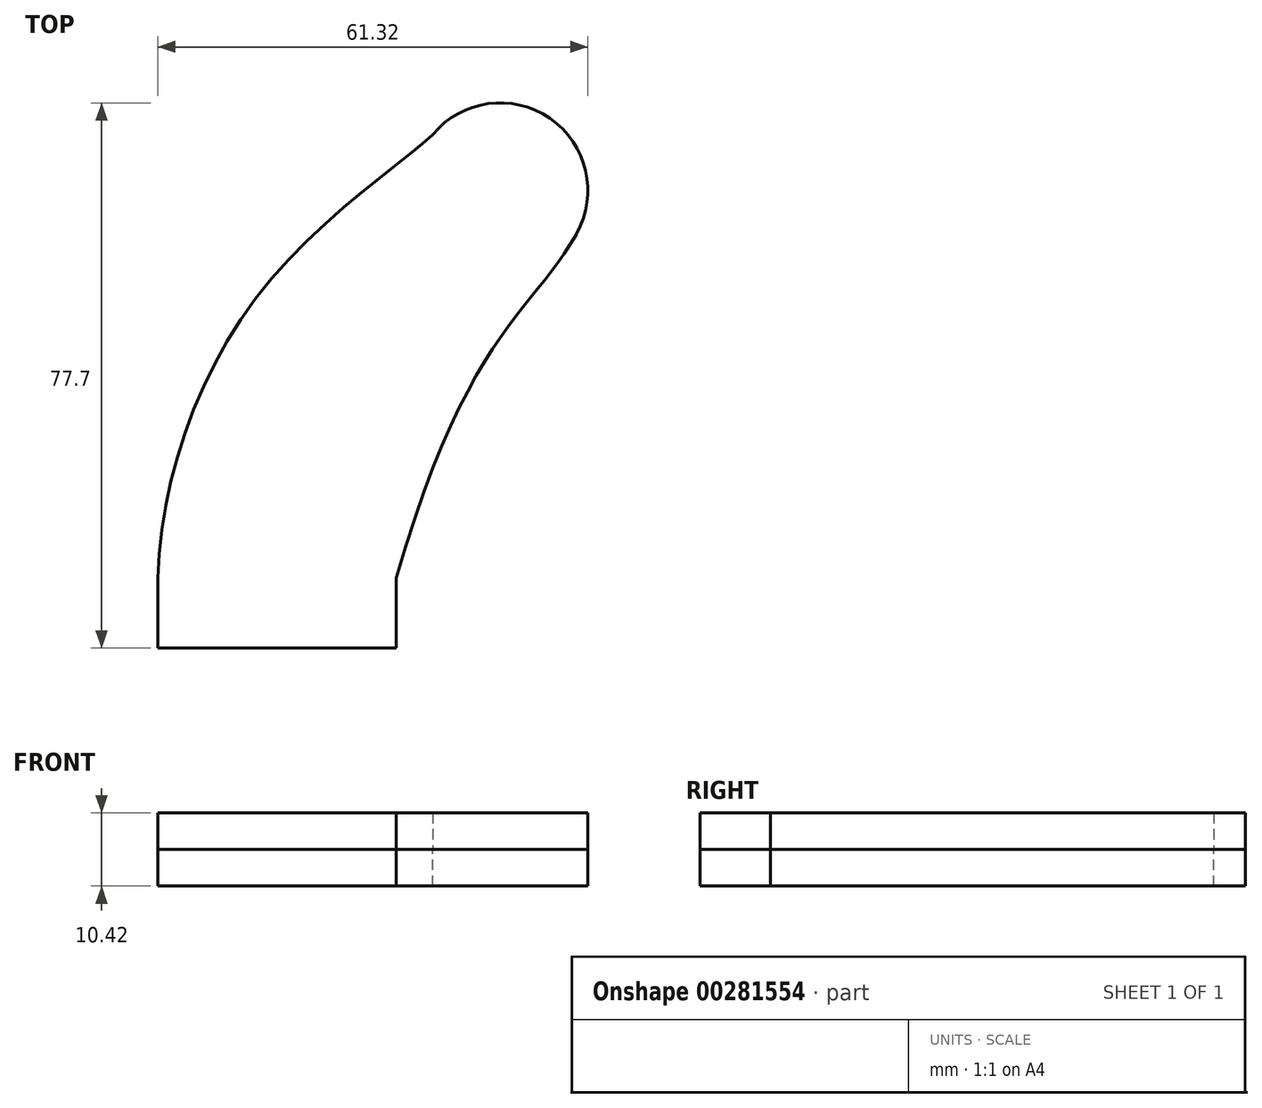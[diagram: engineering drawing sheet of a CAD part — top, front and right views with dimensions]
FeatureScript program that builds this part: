
annotation { "Feature Type Name" : "Feature", "Feature Type Description" : "" }
export const myFeature = defineFeature(function(context is Context, id is Id, definition is map)
    precondition{}
    {
        {
            var Q0;
            Q0=qCreatedBy(makeId("Top.planeOp"),FACE);
            var sketch = newSketch(context, id + "F0", { "sketchPlane" : qUnion([Q0])});
            skCircle(sketch, "E0", {"center": v(14.82, 0) * mm, "radius": 12.5 * mm});
            skLineSegment(sketch, "E1.bottom", {"start": v(-34, -55.2) * mm, "end": v(0, -55.2) * mm});
            skLineSegment(sketch, "E1.top", {"start": v(-34, -65.2) * mm, "end": v(0, -65.2) * mm});
            skLineSegment(sketch, "E1.left", {"start": v(-34, -55.2) * mm, "end": v(-34, -65.2) * mm});
            skLineSegment(sketch, "E1.right", {"start": v(0, -55.2) * mm, "end": v(0, -65.2) * mm});
            skFitSpline(sketch, "E2", {"points": [v(25.7, -6.15) * mm, v(0, -55.2) * mm], "startDerivative": vector(-19.44, -34.34) * mm, "endDerivative": vector(-30.87, -105.94) * mm});
            skFitSpline(sketch, "E3", {"points": [v(-34, -55.2) * mm, v(-17.34, -12.01) * mm, v(6.3, 9.15) * mm], "startDerivative": vector(3.08, 81.99) * mm, "endDerivative": vector(18.38, 23.14) * mm});
            skSolve(sketch);
        }
        {
            var Q0;
            {var subQ4=sQuery(id+"F0.wireOp",EDGE,"E1.bottom");Q0=makeQuery(id+"F0.imprint","IMPRINT",FACE,{"disambiguationData":[TD([[makeQuery(id+"F0.imprint","IMPRINT",EDGE,{"derivedFrom":subQ4}),1.0]])]});}
            var Q1;
            Q1 = qSketchRegion(id + "F0", true);
            extrude(context, id + "F1", {"entities" : qUnion([Q0, Q1]), "depth" : 5.2 * mm});
        }
        {
            var Q0;
            Q0=makeQuery(id+"F1.opExtrude","SWEPT_BODY",BODY,{"disambiguationData":[OSD([sQuery(id+"F0.wireOp",EDGE,"E0"),sQuery(id+"F0.wireOp",EDGE,"E1.top"),sQuery(id+"F0.wireOp",EDGE,"E1.left"),sQuery(id+"F0.wireOp",EDGE,"E1.right"),sQuery(id+"F0.wireOp",EDGE,"E2"),sQuery(id+"F0.wireOp",EDGE,"E3")])]});
            var Q1;
            Q1=qCreatedBy(makeId("Top.planeOp"),FACE);
            mirror(context, id + "F2", {"entities" : qUnion([Q0]), "mirrorPlane" : qUnion([Q1])});
        }
    });
